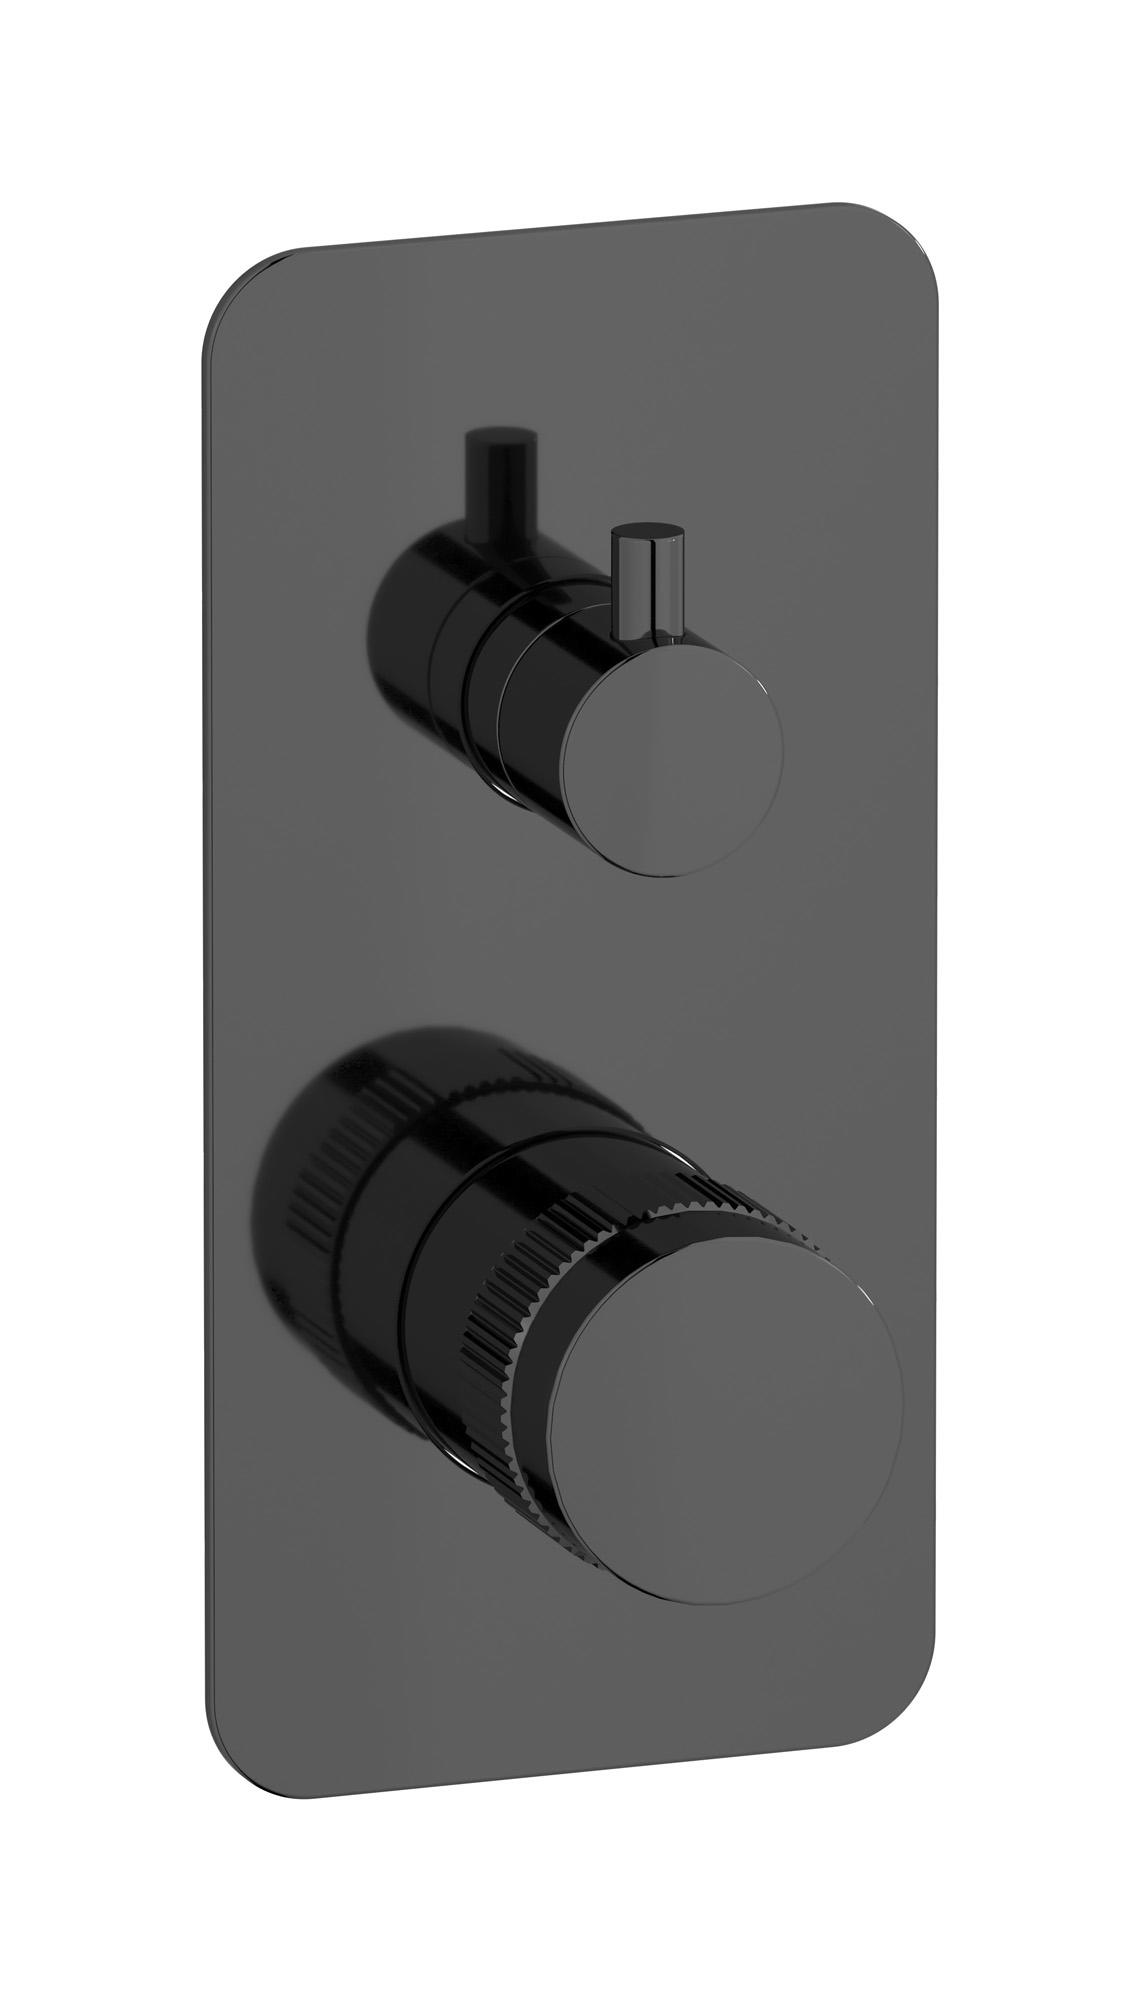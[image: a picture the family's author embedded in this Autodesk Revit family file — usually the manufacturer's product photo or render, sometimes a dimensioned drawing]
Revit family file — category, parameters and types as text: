
# Revit family: RX312
name_source: partatom
category: Apparecchi idraulici
units: mm (PartAtom-declared; Revit-internal decimal feet)

## family parameters
Basato su piano di lavoro = No
Condiviso = No
Mantieni orientamento annotazione = No
Numero OmniClass = 23.45.55.17
Punto di calcolo locali = No
Quota connettore circolare = Usa diametro
Sempre verticale = Sì
Taglio con vuoti quando caricato = No
Tipo di parte = Normale
Titolo OmniClass = Mixing Faucets

## types (12) — shared parameters
Cold water inlet = 10 mm  [stored 0.0328084 ft]
Commenti sul tipo = Exposed parts for manual wall hydroprogressive mixer with 3 ways diverter
Connessione CW = No
Connessione HW = No
Connessione di scarico = No
Connessione di ventilazione = No
Descrizione = Exposed parts for manual wall hydroprogressive mixer with 3 ways diverter
Hot water inlet = 10 mm  [stored 0.0328084 ft]
Produttore = IB Rubinetterie S.p.A.
URL = https://www.weareib.it
zero-valued in all types: Prospetto di default

## per-type parameters (varying)
| type | Finishes surface | Immagine tipo | Modello |
| Chrome | IB_Chrome | RX312CC.jpg | RX312CC |
| Black Chrome | IB_Black chrome | RX312CF.jpg | RX312CF |
| Brushed Black Chrome | IB_Brushed black chrome | RX312CS.jpg | RX312CS |
| Pale Gold | IB_Pale gold | RX312II.jpg | RX312II |
| Brushed Pale Gold | IB_brushed pale gold | RX312IS.jpg | RX312IS |
| Matt Black | IB_matt black | RX312NP.jpg | RX312NP |
| Natural Brass | IB_Brass | RX312ON.jpg | RX312ON |
| Gold | IB_gold | RX312OO.jpg | RX312OO |
| Brushed Gold | IB_brushed gold | RX312OS.jpg | RX312OS |
| Rose Gold | IB_Rose gold | RX312RS.jpg | RX312RS |
| Brushed Rose Gold | IB_Brushed rose gold | RX312SR.jpg | RX312SR |
| Brushed Nickel | IB_Brushed nickel | RX312SS.jpg | RX312SS |

note: [stored X ft] marks values corroborated as IEEE doubles in the binary element streams (Revit-internal decimal feet)
